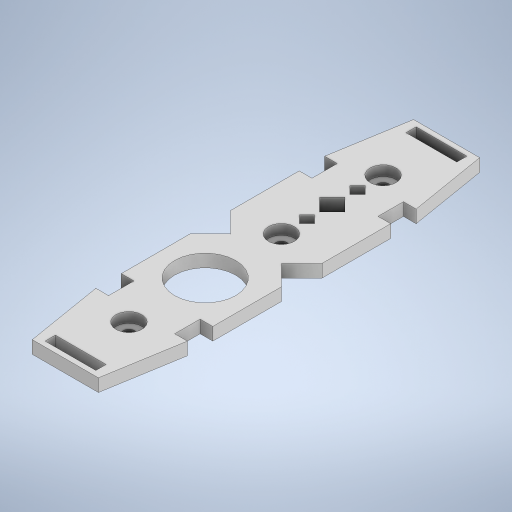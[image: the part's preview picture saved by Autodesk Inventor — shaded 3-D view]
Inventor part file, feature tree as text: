
AUTODESK INVENTOR PART (.ipt)
format: ipt  version: 2023 (Build 270158000, 158)  size: 322,048 bytes
history: native  units: mm
features: extrude x2, sketch x1
ambient origin geometry x8: Origin, YZ Plane, XZ Plane, XY Plane, X Axis, Y Axis, Z Axis, Center Point
bodies: Solid1 (feature_tree)
feature tree (3):
  sketch  "Sketch1"  dims[d4=24.0mm d5=30.0mm d6=10.2mm d7=30.0mm d8=10.2mm d9=40.0mm d12=5.0mm d15=5.0mm d16=10.0mm d17=5.0mm d19=4.5mm d20=4.5mm d21=5.0mm d22=0.0mm d23=1.0mm d24=0.0mm d25=36.0mm d36=3.0mm d37=2.0mm d39=4.0mm d41=2.0mm d42=3.0mm d45=8.0mm d18=0.5mm]
  extrude  "Extrusion1"  Depth=30.0mm
  extrude  "Extrusion2"  Depth=8.0mm
